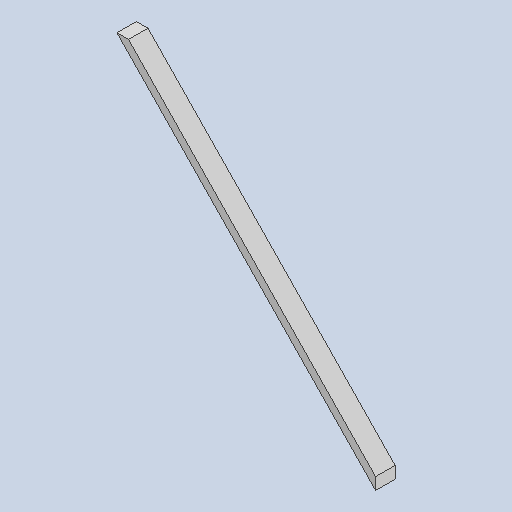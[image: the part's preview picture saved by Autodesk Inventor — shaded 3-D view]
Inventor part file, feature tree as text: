
AUTODESK INVENTOR PART (.ipt)
format: ipt  version: 2025 (Build 290162000, 162)  size: 78,336 bytes
history: native  units: in
note: dims shown in document units (in); Inventor stores cm internally (conversion verified against a paired STEP export)
features: other x3, sketch x1
ambient origin geometry x8: Origin, YZ Plane, XZ Plane, XY Plane, X Axis, Y Axis, Z Axis, Center Point
bodies: Solid1 (feature_tree)
feature tree (4):
  other  "side-side_MIR.ipt"
  other  "Solid1::side-side_MIR.ipt"
  other  "TaggingFeature1"
  sketch  "Sketch1"  dims[d0=0.3937in]
